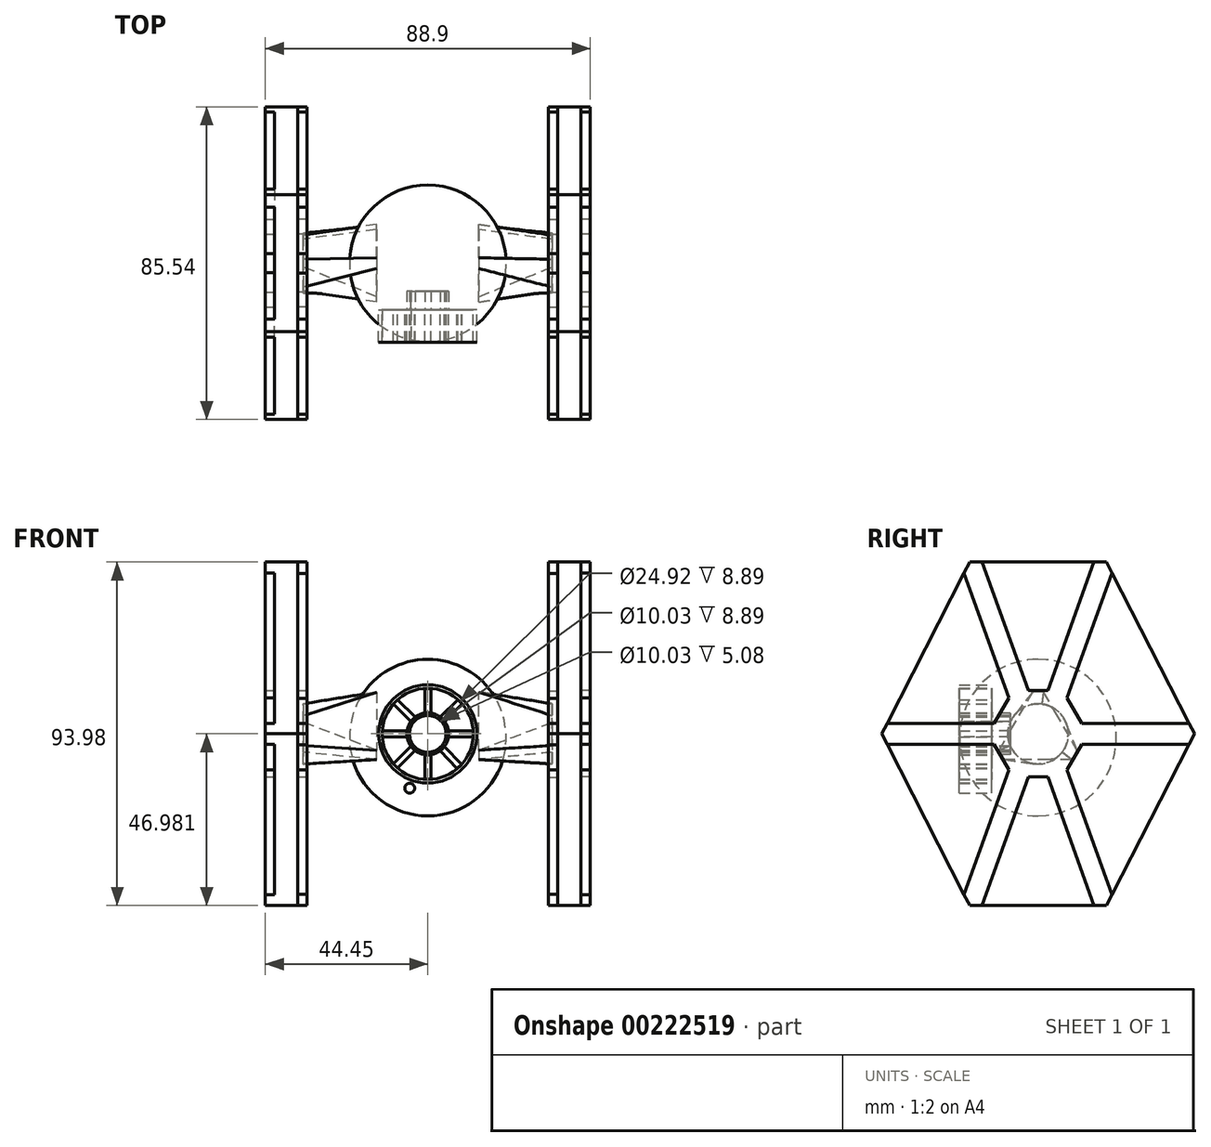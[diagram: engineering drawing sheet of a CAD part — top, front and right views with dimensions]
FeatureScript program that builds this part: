
annotation { "Feature Type Name" : "Feature", "Feature Type Description" : "" }
export const myFeature = defineFeature(function(context is Context, id is Id, definition is map)
    precondition{}
    {
        {
            var Q0;
            Q0=qCreatedBy(makeId("Right.planeOp"),FACE);
            cPlane(context, id + "F0", {"entities" : qUnion([Q0]), "cplaneType" : CPlaneType.OFFSET, "offset" : 38.1 * mm, "width" : 152.4 * mm, "height" : 152.4 * mm});
        }
        {
            var Q0;
            Q0=qCreatedBy(makeId("Right.planeOp"),FACE);
            var sketch = newSketch(context, id + "F1", { "sketchPlane" : qUnion([Q0])});
            skLineSegment(sketch, "E0.bottom", {"start": v(-18.68, -62.8) * mm, "end": v(18.68, -62.8) * mm});
            skPoint(sketch, "E0.middle", {"position": v(0, 0) * mm});
            skLineSegment(sketch, "E1", {"start": v(18.68, -62.8) * mm, "end": v(42.77, -15.81) * mm});
            skLineSegment(sketch, "E2.MirrorCS", {"start": v(-18.68, -62.8) * mm, "end": v(-42.77, -15.81) * mm});
            skLineSegment(sketch, "E3.MirrorCS", {"start": v(18.68, 31.18) * mm, "end": v(42.77, -15.81) * mm});
            skLineSegment(sketch, "E4.MirrorCS", {"start": v(-18.68, 31.18) * mm, "end": v(-42.77, -15.81) * mm});
            skLineSegment(sketch, "E5.MirrorCS", {"start": v(-18.68, 31.18) * mm, "end": v(18.68, 31.18) * mm});
            skSolve(sketch);
        }
        {
            var Q0;
            {var subQ1=sQuery(id+"F1.wireOp",EDGE,"E1");Q0=makeQuery(id+"F1.imprint","IMPRINT",FACE,{"disambiguationData":[TD([[makeQuery(id+"F1.imprint","IMPRINT",EDGE,{"derivedFrom":subQ1}),1.0]])]});}
            extrude(context, id + "F2", {"entities" : qUnion([Q0]), "depth" : 2.54 * mm});
        }
        {
            var Q0;
            Q0=makeQuery(id+"F2.opExtrude","CAP_FACE",FACE,{"disambiguationData":[OSD([sQuery(id+"F1.wireOp",EDGE,"E0.bottom"),sQuery(id+"F1.wireOp",EDGE,"E1"),sQuery(id+"F1.wireOp",EDGE,"E2.MirrorCS"),sQuery(id+"F1.wireOp",EDGE,"E3.MirrorCS"),sQuery(id+"F1.wireOp",EDGE,"E4.MirrorCS"),sQuery(id+"F1.wireOp",EDGE,"E5.MirrorCS"),sQuery(id+"F1.wireOp",EDGE,"2yPUHzrf-kxil-xjin-D1f0-5rGPGX8mDLb6.bottom"),sQuery(id+"F1.wireOp",EDGE,"2yPUHzrf-kxil-xjin-D1f0-5rGPGX8mDLb6.top")])],"isStart":false});
            var sketch = newSketch(context, id + "F3", { "sketchPlane" : qUnion([Q0])});
            skCircle(sketch, "E6", {"center": v(0, -15.81) * mm, "radius": 8.22 * mm});
            skSolve(sketch);
        }
        {
            var Q0;
            Q0=qCreatedBy(id+"F0.planeOp",FACE);
            var sketch = newSketch(context, id + "F4", { "sketchPlane" : qUnion([Q0])});
            skLineSegment(sketch, "E7", {"start": v(-0.03, 4.57) * mm, "end": v(0, -38.27) * mm});
            skArc(sketch, "E8", {"start": v(0, -38.27) * mm, "mid": v(21.4, -16.83) * mm, "end": v(-0.03, 4.57) * mm});
            skSolve(sketch);
        }
        {
            var Q0;
            Q0=makeQuery(id+"F2.opExtrude","CAP_FACE",FACE,{"disambiguationData":[OSD([sQuery(id+"F1.wireOp",EDGE,"E0.bottom"),sQuery(id+"F1.wireOp",EDGE,"E1"),sQuery(id+"F1.wireOp",EDGE,"E2.MirrorCS"),sQuery(id+"F1.wireOp",EDGE,"E3.MirrorCS"),sQuery(id+"F1.wireOp",EDGE,"E4.MirrorCS"),sQuery(id+"F1.wireOp",EDGE,"E5.MirrorCS")])],"isStart":true});
            var sketch = newSketch(context, id + "F5", { "sketchPlane" : qUnion([Q0])});
            skPoint(sketch, "E9.startSnap0", {"position": v(-5.35, -21.22) * mm});
            skSolve(sketch);
        }
        {
            var Q0;
            {var subQ1=sQuery(id+"F5.wireOp",EDGE,"249c2ce5-009a-41f7-bdd2-0ea9e0032ecc0.MirrorCS");var subQ6=makeQuery(id+"F2.opExtrude","CAP_EDGE",EDGE,{"disambiguationData":[OSD([sQuery(id+"F1.wireOp",EDGE,"E5.MirrorCS")])],"isStart":true});var subQ7=makeQuery(id+"F5.imprint","INTERSECT",VERTEX,{"derivedFrom":[subQ6,subQ1]});Q0=makeQuery(id+"F5.imprint","IMPRINT",FACE,{"disambiguationData":[TD([[makeQuery(id+"F5.imprint","IMPRINT",EDGE,{"disambiguationData":[TD([[subQ7,1.0]])],"derivedFrom":subQ6}),1.0]])]});}
            var Q1;
            {var subQ5=sQuery(id+"F5.wireOp",EDGE,"7VcF6iJS-dFkr-JtMG-80JM-9HORZD5tUdc8");Q1=makeQuery(id+"F5.imprint","IMPRINT",FACE,{"disambiguationData":[TD([[makeQuery(id+"F5.imprint","IMPRINT",EDGE,{"derivedFrom":subQ5}),-1.0]])]});}
            var Q2;
            {var subQ1=sQuery(id+"F5.wireOp",EDGE,"d53f9717-c929-49ff-bc3e-877c035910c40.MirrorCS");Q2=makeQuery(id+"F5.imprint","IMPRINT",FACE,{"disambiguationData":[TD([[makeQuery(id+"F5.imprint","IMPRINT",EDGE,{"derivedFrom":subQ1}),1.0]])]});}
            var Q3;
            {var subQ6=sQuery(id+"F5.wireOp",EDGE,"7JM50K66-Pmk8-nCnD-PpWn-c26iKmBIX4QO");var subQ9=sQuery(id+"F5.wireOp",EDGE,"93c2cfdc-00f6-405e-850a-5c9138fb73d70.MirrorC");var subQ11=makeQuery(id+"F5.imprint","INTERSECT",VERTEX,{"disambiguationData":[OD(0.0)],"derivedFrom":[subQ6,subQ9]});Q3=makeQuery(id+"F5.imprint","IMPRINT",FACE,{"disambiguationData":[TD([[makeQuery(id+"F5.imprint","IMPRINT",EDGE,{"disambiguationData":[TD([[subQ11,1.0]])],"derivedFrom":subQ9}),1.0]])]});}
            var Q4;
            {var subQ5=sQuery(id+"F5.wireOp",EDGE,"SASZ7VG5-cB94-bOMo-KIGx-b2qRhCJ8Sax1");Q4=makeQuery(id+"F5.imprint","IMPRINT",FACE,{"disambiguationData":[TD([[makeQuery(id+"F5.imprint","IMPRINT",EDGE,{"derivedFrom":subQ5}),1.0]])]});}
            var Q5;
            {var subQ0=sQuery(id+"F5.wireOp",EDGE,"HNDO0rkw-yRAK-74Ev-MwU3-I7vDTjC7gBuG");Q5=makeQuery(id+"F5.imprint","IMPRINT",FACE,{"disambiguationData":[TD([[makeQuery(id+"F5.imprint","IMPRINT",EDGE,{"derivedFrom":subQ0}),1.0]])]});}
            var Q6;
            {var subQ5=sQuery(id+"F5.wireOp",EDGE,"lByyAeW6-gkVC-xfzd-ToIX-et6EqGNpYPVb");Q6=makeQuery(id+"F5.imprint","IMPRINT",FACE,{"disambiguationData":[TD([[makeQuery(id+"F5.imprint","IMPRINT",EDGE,{"derivedFrom":subQ5}),-1.0]])]});}
            var Q7;
            {var subQ1=sQuery(id+"F5.wireOp",EDGE,"4a8b6011-c6cb-4acc-bbb3-d66b1ed156a90.MirrorCS");Q7=makeQuery(id+"F5.imprint","IMPRINT",FACE,{"disambiguationData":[TD([[makeQuery(id+"F5.imprint","IMPRINT",EDGE,{"derivedFrom":subQ1}),1.0]])]});}
            var Q8;
            {var subQ5=sQuery(id+"F5.wireOp",EDGE,"69e1f89e-e92b-4090-8e51-5caf598a36f10.MirrorCS");Q8=makeQuery(id+"F5.imprint","IMPRINT",FACE,{"disambiguationData":[TD([[makeQuery(id+"F5.imprint","IMPRINT",EDGE,{"derivedFrom":subQ5}),1.0]])]});}
            extrude(context, id + "F6", {"entities" : qUnion([Q0, Q1, Q2, Q3, Q4, Q5, Q6, Q7, Q8]), "operationType" : NewBodyOperationType.ADD, "depth" : 3.8 * mm});
        }
        {
            var Q0;
            Q0=qCreatedBy(makeId("Front.planeOp"),FACE);
            cPlane(context, id + "F7", {"entities" : qUnion([Q0]), "cplaneType" : CPlaneType.OFFSET, "offset" : 12.7 * mm, "width" : 152.4 * mm, "height" : 152.4 * mm});
        }
        {
            var Q0;
            Q0=makeQuery(id+"F2.opExtrude","SWEPT_BODY",BODY,{"disambiguationData":[OSD([sQuery(id+"F1.wireOp",EDGE,"E0.bottom"),sQuery(id+"F1.wireOp",EDGE,"E1"),sQuery(id+"F1.wireOp",EDGE,"E2.MirrorCS"),sQuery(id+"F1.wireOp",EDGE,"E3.MirrorCS"),sQuery(id+"F1.wireOp",EDGE,"E4.MirrorCS"),sQuery(id+"F1.wireOp",EDGE,"E5.MirrorCS"),sQuery(id+"F1.wireOp",EDGE,"2yPUHzrf-kxil-xjin-D1f0-5rGPGX8mDLb6.bottom"),sQuery(id+"F1.wireOp",EDGE,"2yPUHzrf-kxil-xjin-D1f0-5rGPGX8mDLb6.top")])]});
            var Q1;
            Q1=qCreatedBy(id+"F0.planeOp",FACE);
            mirror(context, id + "F8", {"entities" : qUnion([Q0]), "mirrorPlane" : qUnion([Q1])});
        }
        {
            var Q0;
            Q0=qCreatedBy(id+"F7.planeOp",FACE);
            var sketch = newSketch(context, id + "F9", { "sketchPlane" : qUnion([Q0])});
            skLineSegment(sketch, "E10", {"start": v(32.42, -15) * mm, "end": v(32.42, -16.63) * mm});
            skLineSegment(sketch, "E11.MirrorCS", {"start": v(43.78, -15) * mm, "end": v(43.78, -16.63) * mm});
            skCircle(sketch, "E12", {"center": v(38.1, -15.82) * mm, "radius": 5.74 * mm});
            skCircle(sketch, "E13", {"center": v(38.1, -15.82) * mm, "radius": 13.44 * mm});
            skCircle(sketch, "E14", {"center": v(38.1, -15.82) * mm, "radius": 12.46 * mm});
            skLineSegment(sketch, "E15", {"start": v(38.9, -28.25) * mm, "end": v(37.28, -28.25) * mm});
            skLineSegment(sketch, "E16", {"start": v(25.67, -15) * mm, "end": v(25.67, -16.63) * mm});
            skLineSegment(sketch, "E17", {"start": v(25.67, -16.63) * mm, "end": v(32.42, -16.63) * mm});
            skLineSegment(sketch, "E18", {"start": v(25.67, -15) * mm, "end": v(32.42, -15) * mm});
            skLineSegment(sketch, "E19", {"start": v(50.53, -15) * mm, "end": v(50.53, -16.63) * mm});
            skLineSegment(sketch, "E20", {"start": v(43.78, -16.63) * mm, "end": v(50.53, -16.63) * mm});
            skLineSegment(sketch, "E21", {"start": v(43.78, -15) * mm, "end": v(50.53, -15) * mm});
            skPoint(sketch, "E22.startSnap0", {"position": v(43.78, -15.82) * mm});
            skLineSegment(sketch, "E23", {"start": v(28.68, -23.97) * mm, "end": v(29.83, -25.14) * mm});
            skLineSegment(sketch, "E24", {"start": v(28.68, -23.97) * mm, "end": v(33.48, -19.23) * mm});
            skLineSegment(sketch, "E25", {"start": v(29.83, -25.14) * mm, "end": v(34.63, -20.4) * mm});
            skLineSegment(sketch, "E26", {"start": v(34.63, -20.4) * mm, "end": v(33.48, -19.23) * mm});
            skLineSegment(sketch, "E27", {"start": v(37.28, -28.25) * mm, "end": v(37.28, -21.5) * mm});
            skLineSegment(sketch, "E28", {"start": v(38.9, -28.25) * mm, "end": v(38.9, -21.5) * mm});
            skLineSegment(sketch, "E29", {"start": v(38.9, -21.5) * mm, "end": v(37.28, -21.5) * mm});
            skLineSegment(sketch, "E30", {"start": v(37.28, -10.14) * mm, "end": v(38.9, -10.14) * mm});
            skLineSegment(sketch, "E31", {"start": v(37.28, -10.14) * mm, "end": v(37.28, -3.38) * mm});
            skLineSegment(sketch, "E32", {"start": v(38.9, -10.14) * mm, "end": v(38.9, -3.38) * mm});
            skLineSegment(sketch, "E33", {"start": v(38.9, -3.38) * mm, "end": v(37.28, -3.38) * mm});
            skLineSegment(sketch, "E34.MirrorCS", {"start": v(46.37, -6.5) * mm, "end": v(41.57, -11.24) * mm});
            skLineSegment(sketch, "E35.MirrorCS", {"start": v(47.52, -7.66) * mm, "end": v(42.72, -12.4) * mm});
            skLineSegment(sketch, "E36.MirrorCS", {"start": v(42.72, -12.4) * mm, "end": v(41.57, -11.24) * mm});
            skLineSegment(sketch, "E37.MirrorCS", {"start": v(46.37, -6.5) * mm, "end": v(47.52, -7.66) * mm});
            skLineSegment(sketch, "E38.MirrorCS", {"start": v(29.83, -6.5) * mm, "end": v(34.63, -11.24) * mm});
            skLineSegment(sketch, "E39.MirrorCS", {"start": v(28.68, -7.66) * mm, "end": v(33.48, -12.4) * mm});
            skLineSegment(sketch, "E40.MirrorCS", {"start": v(33.48, -12.4) * mm, "end": v(34.63, -11.24) * mm});
            skLineSegment(sketch, "E41.MirrorCS", {"start": v(29.83, -6.5) * mm, "end": v(28.68, -7.66) * mm});
            skLineSegment(sketch, "E42.MirrorCS", {"start": v(47.32, -24.2) * mm, "end": v(42.63, -19.34) * mm});
            skLineSegment(sketch, "E43.MirrorCS", {"start": v(46.14, -25.34) * mm, "end": v(41.46, -20.48) * mm});
            skLineSegment(sketch, "E44.MirrorCS", {"start": v(47.32, -24.2) * mm, "end": v(46.14, -25.34) * mm});
            skLineSegment(sketch, "E45.MirrorCS", {"start": v(41.46, -20.48) * mm, "end": v(42.63, -19.34) * mm});
            skCircle(sketch, "E46", {"center": v(38.1, -15.82) * mm, "radius": 5.01 * mm});
            skSolve(sketch);
        }
        {
            var Q0;
            {var subQ14=sQuery(id+"F9.wireOp",EDGE,"73e59940-f8dd-450e-85ab-330bc53c69c60.MirrorCS");Q0=makeQuery(id+"F9.imprint","IMPRINT",FACE,{"disambiguationData":[TD([[makeQuery(id+"F9.imprint","IMPRINT",EDGE,{"derivedFrom":subQ14}),1.0]])]});}
            var Q1;
            {var subQ0=sQuery(id+"F9.wireOp",EDGE,"sVUFMM5y-C2RM-zDAE-oVfD-lKvkKs6ZE4KX");Q1=makeQuery(id+"F9.imprint","IMPRINT",FACE,{"disambiguationData":[TD([[makeQuery(id+"F9.imprint","IMPRINT",EDGE,{"derivedFrom":subQ0}),1.0]])]});}
            var Q2;
            {var subQ1=sQuery(id+"F9.wireOp",EDGE,"84d815f5-994e-4be1-8628-50fb4fe02ea00.MirrorCS");Q2=makeQuery(id+"F9.imprint","IMPRINT",FACE,{"disambiguationData":[TD([[makeQuery(id+"F9.imprint","IMPRINT",EDGE,{"derivedFrom":subQ1}),1.0]])]});}
            var Q3;
            {var subQ2=sQuery(id+"F9.wireOp",EDGE,"e3cf4e84-a14f-40f9-aafe-2878d3321a520.MirrorCS");Q3=makeQuery(id+"F9.imprint","IMPRINT",FACE,{"disambiguationData":[TD([[makeQuery(id+"F9.imprint","IMPRINT",EDGE,{"derivedFrom":subQ2}),-1.0]])]});}
            var Q4;
            {var subQ1=sQuery(id+"F9.wireOp",EDGE,"E10");Q4=makeQuery(id+"F9.imprint","IMPRINT",FACE,{"disambiguationData":[TD([[makeQuery(id+"F9.imprint","IMPRINT",EDGE,{"derivedFrom":subQ1}),1.0]])]});}
            var Q5;
            {var subQ5=sQuery(id+"F9.wireOp",EDGE,"nq8PGv4s-UvOK-GLhU-MlqA-lW3dcPxD6hmL");Q5=makeQuery(id+"F9.imprint","IMPRINT",FACE,{"disambiguationData":[TD([[makeQuery(id+"F9.imprint","IMPRINT",EDGE,{"derivedFrom":subQ5}),1.0]])]});}
            var Q6;
            Q6=makeQuery(id+"F9.imprint","IMPRINT",FACE,{"disambiguationData":[TD([[makeQuery(id+"F9.imprint","IMPRINT",EDGE,{"derivedFrom":sQuery(id+"F9.wireOp",EDGE,"kJPAYuFo-pbCG-mxDr-NveN-pNAolmRNOq98")}),1.0]])]});
            var Q7;
            {var subQ4=sQuery(id+"F9.wireOp",EDGE,"IcHEI2yc-UJXz-2Fey-pnqX-uZXjIdPkzv1H");Q7=makeQuery(id+"F9.imprint","IMPRINT",FACE,{"disambiguationData":[TD([[makeQuery(id+"F9.imprint","IMPRINT",EDGE,{"derivedFrom":subQ4}),1.0]])]});}
            var Q8;
            {var subQ0=sQuery(id+"F9.wireOp",EDGE,"6c8dea8c-eb7f-4e80-b223-ce5f32e7f4810.MirrorCS");Q8=makeQuery(id+"F9.imprint","IMPRINT",FACE,{"disambiguationData":[TD([[makeQuery(id+"F9.imprint","IMPRINT",EDGE,{"derivedFrom":subQ0}),-1.0]])]});}
            var Q9;
            {var subQ0=sQuery(id+"F9.wireOp",EDGE,"314743cd-5ef3-4182-b27c-d370bf35b7510.MirrorCS");Q9=makeQuery(id+"F9.imprint","IMPRINT",FACE,{"disambiguationData":[TD([[makeQuery(id+"F9.imprint","IMPRINT",EDGE,{"derivedFrom":subQ0}),1.0]])]});}
            extrude(context, id + "F10", {"entities" : qUnion([Q0, Q1, Q2, Q3, Q4, Q5, Q6, Q7, Q8, Q9]), "oppositeDirection" : true, "depth" : 5.08 * mm});
        }
        {
            var Q0;
            Q0=makeQuery(id+"F4.imprint","IMPRINT",FACE,{"disambiguationData":[TD([[makeQuery(id+"F4.imprint","IMPRINT",EDGE,{"derivedFrom":sQuery(id+"F4.wireOp",EDGE,"E7")}),1.0]])]});
            var Q1;
            Q1=sQuery(id+"F4.wireOp",EDGE,"E7");
            revolve(context, id + "F11", {"entities" : qUnion([Q0]), "axis" : qUnion([Q1]), "revolveType" : RevolveType.FULL});
        }
        {
            var Q0;
            {var subQ1=sQuery(id+"F9.wireOp",EDGE,"E38.MirrorCS");Q0=makeQuery(id+"F9.imprint","IMPRINT",FACE,{"disambiguationData":[TD([[makeQuery(id+"F9.imprint","IMPRINT",EDGE,{"derivedFrom":subQ1}),-1.0]])]});}
            var Q1;
            {var subQ0=sQuery(id+"F9.wireOp",EDGE,"E31");Q1=makeQuery(id+"F9.imprint","IMPRINT",FACE,{"disambiguationData":[TD([[makeQuery(id+"F9.imprint","IMPRINT",EDGE,{"derivedFrom":subQ0}),-1.0]])]});}
            var Q2;
            {var subQ1=sQuery(id+"F9.wireOp",EDGE,"E34.MirrorCS");Q2=makeQuery(id+"F9.imprint","IMPRINT",FACE,{"disambiguationData":[TD([[makeQuery(id+"F9.imprint","IMPRINT",EDGE,{"derivedFrom":subQ1}),1.0]])]});}
            var Q3;
            Q3=makeQuery(id+"F9.imprint","IMPRINT",FACE,{"disambiguationData":[TD([[makeQuery(id+"F9.imprint","IMPRINT",EDGE,{"derivedFrom":sQuery(id+"F9.wireOp",EDGE,"E19")}),-1.0]])]});
            var Q4;
            Q4=makeQuery(id+"F9.imprint","IMPRINT",FACE,{"disambiguationData":[TD([[makeQuery(id+"F9.imprint","IMPRINT",EDGE,{"derivedFrom":sQuery(id+"F9.wireOp",EDGE,"E15")}),-1.0]])]});
            var Q5;
            Q5=makeQuery(id+"F9.imprint","IMPRINT",FACE,{"disambiguationData":[TD([[makeQuery(id+"F9.imprint","IMPRINT",EDGE,{"derivedFrom":sQuery(id+"F9.wireOp",EDGE,"E23")}),1.0]])]});
            var Q6;
            {var subQ1=sQuery(id+"F9.wireOp",EDGE,"E42.MirrorCS");Q6=makeQuery(id+"F9.imprint","IMPRINT",FACE,{"disambiguationData":[TD([[makeQuery(id+"F9.imprint","IMPRINT",EDGE,{"derivedFrom":subQ1}),1.0]])]});}
            var Q7;
            Q7=makeQuery(id+"F9.imprint","IMPRINT",FACE,{"disambiguationData":[TD([[makeQuery(id+"F9.imprint","IMPRINT",EDGE,{"derivedFrom":sQuery(id+"F9.wireOp",EDGE,"E16")}),1.0]])]});
            var Q8;
            Q8=makeQuery(id+"F9.imprint","IMPRINT",FACE,{"disambiguationData":[TD([[makeQuery(id+"F9.imprint","IMPRINT",EDGE,{"derivedFrom":sQuery(id+"F9.wireOp",EDGE,"E13")}),1.0]])]});
            var Q9;
            {var subQ5=sQuery(id+"F9.wireOp",EDGE,"E10");Q9=makeQuery(id+"F9.imprint","IMPRINT",FACE,{"disambiguationData":[TD([[makeQuery(id+"F9.imprint","IMPRINT",EDGE,{"derivedFrom":subQ5}),1.0]])]});}
            extrude(context, id + "F12", {"entities" : qUnion([Q0, Q1, Q2, Q3, Q4, Q5, Q6, Q7, Q8, Q9]), "depth" : 8.9 * mm, "offsetDistance" : 25.4 * mm});
        }
        {
            var Q0;
            Q0=qCreatedBy(id+"F7.planeOp",FACE);
            var sketch = newSketch(context, id + "F13", { "sketchPlane" : qUnion([Q0])});
            skCircle(sketch, "E47", {"center": v(33.15, -30.69) * mm, "radius": 1.36 * mm});
            skCircle(sketch, "E48.MirrorC", {"center": v(43.05, -30.69) * mm, "radius": 1.36 * mm});
            skSolve(sketch);
        }
        {
            var Q0;
            Q0=makeQuery(id+"F13.imprint","IMPRINT",FACE,{"disambiguationData":[TD([[makeQuery(id+"F13.imprint","IMPRINT",EDGE,{"derivedFrom":sQuery(id+"F13.wireOp",EDGE,"E47")}),1.0]])]});
            var Q1;
            Q1=makeQuery(id+"F13.imprint","IMPRINT",FACE,{"disambiguationData":[TD([[makeQuery(id+"F13.imprint","IMPRINT",EDGE,{"derivedFrom":sQuery(id+"F13.wireOp",EDGE,"E48.MirrorC")}),-1.0]])]});
            extrude(context, id + "F14", {"entities" : qUnion([Q0, Q1]), "depth" : 8.9 * mm});
        }
        {
            var Q0;
            {var subQ0=sQuery(id+"F1.wireOp",EDGE,"E4.MirrorCS");Q0=makeQuery(id+"F17.boolean.opBoolean","SPLIT",FACE,{"disambiguationData":[TD([makeQuery(id+"F2.opExtrude","SWEPT_FACE",FACE,{"disambiguationData":[OSD([subQ0])]})])],"derivedFrom":makeQuery(id+"F6.opExtrude","CAP_FACE",FACE,{"disambiguationData":[OSD([sQuery(id+"F1.wireOp",EDGE,"E0.bottom"),sQuery(id+"F1.wireOp",EDGE,"E1"),sQuery(id+"F1.wireOp",EDGE,"E2.MirrorCS"),sQuery(id+"F1.wireOp",EDGE,"E3.MirrorCS"),subQ0,sQuery(id+"F1.wireOp",EDGE,"E5.MirrorCS")])],"isStart":false})});}
            cPlane(context, id + "F15", {"entities" : qUnion([Q0]), "cplaneType" : CPlaneType.OFFSET, "offset" : 0 * mm, "width" : 152.4 * mm, "height" : 152.4 * mm});
        }
        {
            var Q0;
            Q0=qCreatedBy(id+"F15.planeOp",FACE);
            var sketch = newSketch(context, id + "F16", { "sketchPlane" : qUnion([Q0])});
            skPoint(sketch, "E49.0.midPoint", {"position": v(0, -24.03) * mm});
            skLineSegment(sketch, "E50", {"start": v(-18.68, -62.8) * mm, "end": v(-20.23, -59.77) * mm});
            skLineSegment(sketch, "E51", {"start": v(-18.68, -62.8) * mm, "end": v(-15.28, -62.8) * mm});
            skLineSegment(sketch, "E52", {"start": v(-20.23, -59.77) * mm, "end": v(-7.97, -25.65) * mm});
            skLineSegment(sketch, "E53", {"start": v(-15.28, -62.8) * mm, "end": v(-2.64, -27.63) * mm});
            skLineSegment(sketch, "E54.MirrorCS", {"start": v(15.28, -62.8) * mm, "end": v(2.64, -27.63) * mm});
            skLineSegment(sketch, "E55.MirrorCS", {"start": v(20.23, -59.77) * mm, "end": v(7.97, -25.65) * mm});
            skLineSegment(sketch, "E56.MirrorCS", {"start": v(18.68, -62.8) * mm, "end": v(15.28, -62.8) * mm});
            skLineSegment(sketch, "E57.MirrorCS", {"start": v(18.68, -62.8) * mm, "end": v(20.23, -59.77) * mm});
            skLineSegment(sketch, "E58.MirrorCS", {"start": v(20.23, 28.14) * mm, "end": v(7.97, -5.98) * mm});
            skLineSegment(sketch, "E59.MirrorCS", {"start": v(15.28, 31.18) * mm, "end": v(2.64, -4) * mm});
            skLineSegment(sketch, "E60.MirrorCS", {"start": v(18.68, 31.18) * mm, "end": v(20.23, 28.14) * mm});
            skLineSegment(sketch, "E61.MirrorCS", {"start": v(18.68, 31.18) * mm, "end": v(15.28, 31.18) * mm});
            skLineSegment(sketch, "E62.MirrorCS", {"start": v(-20.23, 28.14) * mm, "end": v(-7.97, -5.98) * mm});
            skLineSegment(sketch, "E63.MirrorCS", {"start": v(-15.28, 31.18) * mm, "end": v(-2.64, -4) * mm});
            skLineSegment(sketch, "E64.MirrorCS", {"start": v(-18.68, 31.18) * mm, "end": v(-15.28, 31.18) * mm});
            skLineSegment(sketch, "E65.MirrorCS", {"start": v(-18.68, 31.18) * mm, "end": v(-20.23, 28.14) * mm});
            skLineSegment(sketch, "E66", {"start": v(-6.37, -21.2) * mm, "end": v(-1.35, -24.03) * mm});
            skLineSegment(sketch, "E67", {"start": v(1.35, -24.03) * mm, "end": v(6.37, -21.2) * mm});
            skLineSegment(sketch, "E68", {"start": v(-6.37, -10.42) * mm, "end": v(-1.35, -7.6) * mm});
            skLineSegment(sketch, "E69", {"start": v(1.35, -7.6) * mm, "end": v(6.37, -10.42) * mm});
            skLineSegment(sketch, "E70", {"start": v(-41.3, -12.93) * mm, "end": v(-42.77, -15.81) * mm});
            skLineSegment(sketch, "E71", {"start": v(-42.77, -15.81) * mm, "end": v(-41.3, -18.7) * mm});
            skLineSegment(sketch, "E72", {"start": v(-41.3, -12.93) * mm, "end": v(-11.98, -12.93) * mm});
            skLineSegment(sketch, "E73", {"start": v(-41.3, -18.7) * mm, "end": v(-11.98, -18.7) * mm});
            skLineSegment(sketch, "E74", {"start": v(-7.7, -18.7) * mm, "end": v(-7.7, -12.93) * mm});
            skLineSegment(sketch, "E75.MirrorCS", {"start": v(41.3, -12.93) * mm, "end": v(11.98, -12.93) * mm});
            skLineSegment(sketch, "E76.MirrorCS", {"start": v(41.3, -18.7) * mm, "end": v(11.98, -18.7) * mm});
            skLineSegment(sketch, "E77.MirrorCS", {"start": v(7.7, -18.7) * mm, "end": v(7.7, -12.93) * mm});
            skLineSegment(sketch, "E78.MirrorCS", {"start": v(42.77, -15.81) * mm, "end": v(41.3, -18.7) * mm});
            skLineSegment(sketch, "E79.MirrorCS", {"start": v(41.3, -12.93) * mm, "end": v(42.77, -15.81) * mm});
            skLineSegment(sketch, "E80", {"start": v(-7.7, -18.7) * mm, "end": v(-6.37, -21.2) * mm});
            skLineSegment(sketch, "E81", {"start": v(-7.7, -12.93) * mm, "end": v(-6.37, -10.42) * mm});
            skLineSegment(sketch, "E82", {"start": v(-1.35, -7.6) * mm, "end": v(1.35, -7.6) * mm});
            skLineSegment(sketch, "E83", {"start": v(6.37, -10.42) * mm, "end": v(7.7, -12.93) * mm});
            skLineSegment(sketch, "E84", {"start": v(6.37, -21.2) * mm, "end": v(7.7, -18.7) * mm});
            skLineSegment(sketch, "E85", {"start": v(-1.35, -24.03) * mm, "end": v(1.35, -24.03) * mm});
            skLineSegment(sketch, "E86.0", {"start": v(6.82, -27.63) * mm, "end": v(-6.82, -27.63) * mm});
            skLineSegment(sketch, "E86.1", {"start": v(-6.82, -27.63) * mm, "end": v(-13.64, -15.81) * mm});
            skLineSegment(sketch, "E86.2", {"start": v(-13.64, -15.81) * mm, "end": v(-6.82, -4) * mm});
            skLineSegment(sketch, "E86.3", {"start": v(-6.82, -4) * mm, "end": v(6.82, -4) * mm});
            skLineSegment(sketch, "E86.4", {"start": v(6.82, -4) * mm, "end": v(13.64, -15.81) * mm});
            skLineSegment(sketch, "E86.5", {"start": v(13.64, -15.81) * mm, "end": v(6.82, -27.63) * mm});
            skPoint(sketch, "E86.0.midPoint", {"position": v(0, -27.63) * mm});
            skSolve(sketch);
        }
        {
            var Q0;
            Q0=makeQuery(id+"F16.imprint","IMPRINT",FACE,{"disambiguationData":[TD([[makeQuery(id+"F16.imprint","IMPRINT",EDGE,{"derivedFrom":sQuery(id+"F16.wireOp",EDGE,"E70")}),1.0]])]});
            var Q1;
            Q1=makeQuery(id+"F16.imprint","IMPRINT",FACE,{"disambiguationData":[TD([[makeQuery(id+"F16.imprint","IMPRINT",EDGE,{"derivedFrom":sQuery(id+"F16.wireOp",EDGE,"E66")}),1.0]])]});
            var Q2;
            Q2=makeQuery(id+"F16.imprint","IMPRINT",FACE,{"disambiguationData":[TD([[makeQuery(id+"F16.imprint","IMPRINT",EDGE,{"derivedFrom":sQuery(id+"F16.wireOp",EDGE,"E58.MirrorCS")}),-1.0]])]});
            var Q3;
            Q3=makeQuery(id+"F16.imprint","IMPRINT",FACE,{"disambiguationData":[TD([[makeQuery(id+"F16.imprint","IMPRINT",EDGE,{"derivedFrom":sQuery(id+"F16.wireOp",EDGE,"E62.MirrorCS")}),1.0]])]});
            var Q4;
            Q4=makeQuery(id+"F16.imprint","IMPRINT",FACE,{"disambiguationData":[TD([[makeQuery(id+"F16.imprint","IMPRINT",EDGE,{"derivedFrom":sQuery(id+"F16.wireOp",EDGE,"E75.MirrorCS")}),1.0]])]});
            var Q5;
            Q5=makeQuery(id+"F16.imprint","IMPRINT",FACE,{"disambiguationData":[TD([[makeQuery(id+"F16.imprint","IMPRINT",EDGE,{"derivedFrom":sQuery(id+"F16.wireOp",EDGE,"E54.MirrorCS")}),-1.0]])]});
            var Q6;
            Q6=makeQuery(id+"F16.imprint","IMPRINT",FACE,{"disambiguationData":[TD([[makeQuery(id+"F16.imprint","IMPRINT",EDGE,{"derivedFrom":sQuery(id+"F16.wireOp",EDGE,"E50")}),-1.0]])]});
            var Q7;
            Q7=makeQuery(id+"F16.imprint","IMPRINT",FACE,{"disambiguationData":[TD([[makeQuery(id+"F16.imprint","IMPRINT",EDGE,{"derivedFrom":sQuery(id+"F16.wireOp",EDGE,"E66")}),-1.0]])]});
            extrude(context, id + "F17", {"entities" : qUnion([Q0, Q1, Q2, Q3, Q4, Q5, Q6, Q7]), "operationType" : NewBodyOperationType.ADD, "depth" : 2.54 * mm});
        }
        {
            var Q0;
            Q0=makeQuery(id+"F2.opExtrude","SWEPT_BODY",BODY,{"disambiguationData":[OSD([sQuery(id+"F1.wireOp",EDGE,"E0.bottom"),sQuery(id+"F1.wireOp",EDGE,"E1"),sQuery(id+"F1.wireOp",EDGE,"E2.MirrorCS"),sQuery(id+"F1.wireOp",EDGE,"E3.MirrorCS"),sQuery(id+"F1.wireOp",EDGE,"E4.MirrorCS"),sQuery(id+"F1.wireOp",EDGE,"E5.MirrorCS")])]});
            var Q1;
            Q1=qCreatedBy(id+"F0.planeOp",FACE);
            mirror(context, id + "F18", {"entities" : qUnion([Q0]), "mirrorPlane" : qUnion([Q1])});
        }
        {
            var Q0;
            Q0=makeQuery(id+"F3.imprint","IMPRINT",FACE,{"disambiguationData":[TD([[makeQuery(id+"F3.imprint","IMPRINT",EDGE,{"derivedFrom":sQuery(id+"F3.wireOp",EDGE,"E6")}),-1.0]])]});
            var sketch = newSketch(context, id + "F19", { "sketchPlane" : qUnion([Q0])});
            skPoint(sketch, "E87.0.midPoint", {"position": v(-0.03, -24.09) * mm});
            skLineSegment(sketch, "E88", {"start": v(-18.73, -62.91) * mm, "end": v(-20.29, -59.88) * mm});
            skLineSegment(sketch, "E89", {"start": v(-18.73, -62.91) * mm, "end": v(-15.33, -62.91) * mm});
            skLineSegment(sketch, "E90", {"start": v(-20.29, -59.88) * mm, "end": v(-7.98, -25.63) * mm});
            skLineSegment(sketch, "E91", {"start": v(-15.33, -62.91) * mm, "end": v(-2.66, -27.65) * mm});
            skLineSegment(sketch, "E92.MirrorCS", {"start": v(15.27, -62.91) * mm, "end": v(2.6, -27.65) * mm});
            skLineSegment(sketch, "E93.MirrorCS", {"start": v(20.23, -59.88) * mm, "end": v(7.95, -25.7) * mm});
            skLineSegment(sketch, "E94.MirrorCS", {"start": v(18.67, -62.91) * mm, "end": v(15.27, -62.91) * mm});
            skLineSegment(sketch, "E95.MirrorCS", {"start": v(18.67, -62.91) * mm, "end": v(20.23, -59.88) * mm});
            skLineSegment(sketch, "E96.MirrorCS", {"start": v(20.23, 28.16) * mm, "end": v(7.96, -6) * mm});
            skLineSegment(sketch, "E97.MirrorCS", {"start": v(15.27, 31.2) * mm, "end": v(2.61, -4.02) * mm});
            skLineSegment(sketch, "E98.MirrorCS", {"start": v(18.67, 31.2) * mm, "end": v(20.23, 28.16) * mm});
            skLineSegment(sketch, "E99.MirrorCS", {"start": v(18.67, 31.2) * mm, "end": v(15.27, 31.2) * mm});
            skLineSegment(sketch, "E100.MirrorCS", {"start": v(-20.29, 28.16) * mm, "end": v(-8, -6.06) * mm});
            skLineSegment(sketch, "E101.MirrorCS", {"start": v(-15.33, 31.2) * mm, "end": v(-2.68, -4.02) * mm});
            skLineSegment(sketch, "E102.MirrorCS", {"start": v(-18.73, 31.2) * mm, "end": v(-15.33, 31.2) * mm});
            skLineSegment(sketch, "E103.MirrorCS", {"start": v(-18.73, 31.2) * mm, "end": v(-20.29, 28.16) * mm});
            skLineSegment(sketch, "E104", {"start": v(-41.38, -12.97) * mm, "end": v(-42.86, -15.86) * mm});
            skLineSegment(sketch, "E105", {"start": v(-42.86, -15.86) * mm, "end": v(-41.38, -18.75) * mm});
            skLineSegment(sketch, "E106", {"start": v(-41.38, -12.97) * mm, "end": v(-11.99, -12.97) * mm});
            skLineSegment(sketch, "E107", {"start": v(-41.38, -18.75) * mm, "end": v(-11.96, -18.75) * mm});
            skLineSegment(sketch, "E108.MirrorCS", {"start": v(41.32, -12.97) * mm, "end": v(11.99, -12.97) * mm});
            skLineSegment(sketch, "E109.MirrorCS", {"start": v(41.32, -18.75) * mm, "end": v(11.96, -18.75) * mm});
            skLineSegment(sketch, "E110.MirrorCS", {"start": v(42.8, -15.86) * mm, "end": v(41.32, -18.75) * mm});
            skLineSegment(sketch, "E111.MirrorCS", {"start": v(41.32, -12.97) * mm, "end": v(42.8, -15.86) * mm});
            skLineSegment(sketch, "E112.0", {"start": v(6.82, -27.65) * mm, "end": v(-6.82, -27.65) * mm});
            skLineSegment(sketch, "E112.1", {"start": v(-6.82, -27.65) * mm, "end": v(-13.64, -15.84) * mm});
            skLineSegment(sketch, "E112.2", {"start": v(-13.64, -15.84) * mm, "end": v(-6.82, -4.02) * mm});
            skLineSegment(sketch, "E112.3", {"start": v(-6.82, -4.02) * mm, "end": v(6.82, -4.02) * mm});
            skLineSegment(sketch, "E112.4", {"start": v(6.82, -4.02) * mm, "end": v(13.64, -15.84) * mm});
            skLineSegment(sketch, "E112.5", {"start": v(13.64, -15.84) * mm, "end": v(6.82, -27.65) * mm});
            skPoint(sketch, "E112.0.midPoint", {"position": v(0, -27.65) * mm});
            skSolve(sketch);
        }
        {
            var Q0;
            {var subQ0=sQuery(id+"F19.wireOp",EDGE,"E112.1");var subQ1=sQuery(id+"F19.wireOp",EDGE,"E90");var subQ2=makeQuery(id+"F19.imprint","INTERSECT",VERTEX,{"derivedFrom":[subQ1,subQ0]});Q0=makeQuery(id+"F19.imprint","IMPRINT",FACE,{"disambiguationData":[TD([[makeQuery(id+"F19.imprint","IMPRINT",EDGE,{"disambiguationData":[TD([[subQ2,1.0]])],"derivedFrom":subQ1}),-1.0]])]});}
            var Q1;
            {var subQ3=sQuery(id+"F19.wireOp",EDGE,"E112.2");var subQ9=sQuery(id+"F19.wireOp",EDGE,"E106");var subQ10=makeQuery(id+"F19.imprint","INTERSECT",VERTEX,{"derivedFrom":[subQ9,subQ3]});Q1=makeQuery(id+"F19.imprint","IMPRINT",FACE,{"disambiguationData":[TD([[makeQuery(id+"F19.imprint","IMPRINT",EDGE,{"disambiguationData":[TD([[subQ10,1.0]])],"derivedFrom":subQ9}),-1.0]])]});}
            var Q2;
            {var subQ3=sQuery(id+"F19.wireOp",EDGE,"E112.4");var subQ7=sQuery(id+"F19.wireOp",EDGE,"E96.MirrorCS");var subQ8=makeQuery(id+"F19.imprint","INTERSECT",VERTEX,{"derivedFrom":[subQ7,subQ3]});Q2=makeQuery(id+"F19.imprint","IMPRINT",FACE,{"disambiguationData":[TD([[makeQuery(id+"F19.imprint","IMPRINT",EDGE,{"disambiguationData":[TD([[subQ8,1.0]])],"derivedFrom":subQ7}),-1.0]])]});}
            var Q3;
            {var subQ0=sQuery(id+"F19.wireOp",EDGE,"E112.4");var subQ1=sQuery(id+"F19.wireOp",EDGE,"E108.MirrorCS");var subQ2=makeQuery(id+"F19.imprint","INTERSECT",VERTEX,{"derivedFrom":[subQ1,subQ0]});Q3=makeQuery(id+"F19.imprint","IMPRINT",FACE,{"disambiguationData":[TD([[makeQuery(id+"F19.imprint","IMPRINT",EDGE,{"disambiguationData":[TD([[subQ2,1.0]])],"derivedFrom":subQ1}),1.0]])]});}
            var Q4;
            {var subQ3=sQuery(id+"F19.wireOp",EDGE,"E112.2");var subQ7=sQuery(id+"F19.wireOp",EDGE,"E100.MirrorCS");var subQ8=makeQuery(id+"F19.imprint","INTERSECT",VERTEX,{"derivedFrom":[subQ7,subQ3]});Q4=makeQuery(id+"F19.imprint","IMPRINT",FACE,{"disambiguationData":[TD([[makeQuery(id+"F19.imprint","IMPRINT",EDGE,{"disambiguationData":[TD([[subQ8,1.0]])],"derivedFrom":subQ7}),1.0]])]});}
            var Q5;
            Q5=makeQuery(id+"F19.imprint","IMPRINT",FACE,{"disambiguationData":[TD([[makeQuery(id+"F19.imprint","IMPRINT",EDGE,{"derivedFrom":makeQuery(id+"F3.imprint","IMPRINT",EDGE,{"derivedFrom":sQuery(id+"F3.wireOp",EDGE,"E6")})}),-1.0]])]});
            var Q6;
            Q6=makeQuery(id+"F19.imprint","IMPRINT",FACE,{"disambiguationData":[TD([[makeQuery(id+"F19.imprint","IMPRINT",EDGE,{"derivedFrom":makeQuery(id+"F3.imprint","IMPRINT",EDGE,{"derivedFrom":sQuery(id+"F3.wireOp",EDGE,"E6")})}),1.0]])]});
            var Q7;
            {var subQ3=sQuery(id+"F19.wireOp",EDGE,"E112.0");var subQ7=sQuery(id+"F19.wireOp",EDGE,"E92.MirrorCS");var subQ8=makeQuery(id+"F19.imprint","INTERSECT",VERTEX,{"derivedFrom":[subQ7,subQ3]});Q7=makeQuery(id+"F19.imprint","IMPRINT",FACE,{"disambiguationData":[TD([[makeQuery(id+"F19.imprint","IMPRINT",EDGE,{"disambiguationData":[TD([[subQ8,1.0]])],"derivedFrom":subQ7}),-1.0]])]});}
            extrude(context, id + "F20", {"entities" : qUnion([Q0, Q1, Q2, Q3, Q4, Q5, Q6, Q7]), "depth" : 2.54 * mm, "offsetDistance" : 25.4 * mm});
        }
        {
            var Q0;
            Q0=makeQuery(id+"F20.opExtrude","SWEPT_BODY",BODY,{"disambiguationData":[OSD([sQuery(id+"F1.wireOp",EDGE,"E2.MirrorCS"),sQuery(id+"F1.wireOp",EDGE,"E4.MirrorCS"),sQuery(id+"F3.wireOp",EDGE,"E6"),sQuery(id+"F19.wireOp",EDGE,"E106"),sQuery(id+"F19.wireOp",EDGE,"E107"),sQuery(id+"F19.wireOp",EDGE,"2aa20023-c7b0-4b2b-915d-71bae8cab18d")])]});
            var Q1;
            Q1=makeQuery(id+"F20.opExtrude","SWEPT_BODY",BODY,{"disambiguationData":[OSD([sQuery(id+"F3.wireOp",EDGE,"E6")])]});
            var Q2;
            Q2=makeQuery(id+"F20.opExtrude","SWEPT_BODY",BODY,{"disambiguationData":[OSD([sQuery(id+"F1.wireOp",EDGE,"E4.MirrorCS"),sQuery(id+"F3.wireOp",EDGE,"E6"),sQuery(id+"F19.wireOp",EDGE,"E100.MirrorCS"),sQuery(id+"F19.wireOp",EDGE,"E101.MirrorCS"),sQuery(id+"F19.wireOp",EDGE,"E102.MirrorCS"),sQuery(id+"F19.wireOp",EDGE,"7af6e436-8d5a-4fc4-bd95-5afbcdf9ebc1")])]});
            var Q3;
            Q3=makeQuery(id+"F20.opExtrude","SWEPT_BODY",BODY,{"disambiguationData":[OSD([sQuery(id+"F3.wireOp",EDGE,"E6"),sQuery(id+"F19.wireOp",EDGE,"E96.MirrorCS"),sQuery(id+"F19.wireOp",EDGE,"E97.MirrorCS"),sQuery(id+"F19.wireOp",EDGE,"E98.MirrorCS"),sQuery(id+"F19.wireOp",EDGE,"E99.MirrorCS"),sQuery(id+"F19.wireOp",EDGE,"c8762eaa-3f5d-43dd-ad10-f707925b9254")])]});
            var Q4;
            Q4=makeQuery(id+"F20.opExtrude","SWEPT_BODY",BODY,{"disambiguationData":[OSD([sQuery(id+"F1.wireOp",EDGE,"E0.bottom"),sQuery(id+"F1.wireOp",EDGE,"E2.MirrorCS"),sQuery(id+"F3.wireOp",EDGE,"E6"),sQuery(id+"F19.wireOp",EDGE,"E90"),sQuery(id+"F19.wireOp",EDGE,"E91"),sQuery(id+"F19.wireOp",EDGE,"dfccf998-6865-4125-a587-a97a453d0cde")])]});
            var Q5;
            Q5=makeQuery(id+"F20.opExtrude","SWEPT_BODY",BODY,{"disambiguationData":[OSD([sQuery(id+"F1.wireOp",EDGE,"E0.bottom"),sQuery(id+"F3.wireOp",EDGE,"E6"),sQuery(id+"F19.wireOp",EDGE,"E92.MirrorCS"),sQuery(id+"F19.wireOp",EDGE,"E93.MirrorCS"),sQuery(id+"F19.wireOp",EDGE,"E95.MirrorCS"),sQuery(id+"F19.wireOp",EDGE,"cf72e361-4477-4e51-9806-6e20ddd057b3")])]});
            var Q6;
            Q6=makeQuery(id+"F20.opExtrude","SWEPT_BODY",BODY,{"disambiguationData":[OSD([sQuery(id+"F3.wireOp",EDGE,"E6"),sQuery(id+"F19.wireOp",EDGE,"E108.MirrorCS"),sQuery(id+"F19.wireOp",EDGE,"E109.MirrorCS"),sQuery(id+"F19.wireOp",EDGE,"E110.MirrorCS"),sQuery(id+"F19.wireOp",EDGE,"E111.MirrorCS")])]});
            var Q7;
            Q7=qCreatedBy(id+"F0.planeOp",FACE);
            mirror(context, id + "F21", {"entities" : qUnion([Q0, Q1, Q2, Q3, Q4, Q5, Q6]), "mirrorPlane" : qUnion([Q7])});
        }
        {
            var Q0;
            Q0=qCreatedBy(makeId("Right.planeOp"),FACE);
            cPlane(context, id + "F22", {"entities" : qUnion([Q0]), "cplaneType" : CPlaneType.OFFSET, "offset" : 24.13 * mm, "width" : 152.4 * mm, "height" : 152.4 * mm});
        }
        {
            var Q0;
            Q0=qCreatedBy(id+"F0.planeOp",FACE);
            cPlane(context, id + "F23", {"entities" : qUnion([Q0]), "cplaneType" : CPlaneType.OFFSET, "offset" : 34.04 * mm, "oppositeDirection" : true, "width" : 152.4 * mm, "height" : 152.4 * mm});
        }
        {
            var Q0;
            Q0=makeQuery(id+"F20.opExtrude","SWEPT_BODY",BODY,{"disambiguationData":[OSD([sQuery(id+"F1.wireOp",EDGE,"E0.bottom"),sQuery(id+"F1.wireOp",EDGE,"E2.MirrorCS"),sQuery(id+"F1.wireOp",EDGE,"E4.MirrorCS"),sQuery(id+"F3.wireOp",EDGE,"E6"),sQuery(id+"F19.wireOp",EDGE,"E90"),sQuery(id+"F19.wireOp",EDGE,"E91"),sQuery(id+"F19.wireOp",EDGE,"E92.MirrorCS"),sQuery(id+"F19.wireOp",EDGE,"E93.MirrorCS"),sQuery(id+"F19.wireOp",EDGE,"E94.MirrorCS"),sQuery(id+"F19.wireOp",EDGE,"E95.MirrorCS"),sQuery(id+"F19.wireOp",EDGE,"E96.MirrorCS"),sQuery(id+"F19.wireOp",EDGE,"E97.MirrorCS"),sQuery(id+"F19.wireOp",EDGE,"E98.MirrorCS"),sQuery(id+"F19.wireOp",EDGE,"E99.MirrorCS"),sQuery(id+"F19.wireOp",EDGE,"E100.MirrorCS"),sQuery(id+"F19.wireOp",EDGE,"E101.MirrorCS"),sQuery(id+"F19.wireOp",EDGE,"E102.MirrorCS"),sQuery(id+"F19.wireOp",EDGE,"E103.MirrorCS"),sQuery(id+"F19.wireOp",EDGE,"dfccf998-6865-4125-a587-a97a453d0cde"),sQuery(id+"F19.wireOp",EDGE,"cf72e361-4477-4e51-9806-6e20ddd057b3"),sQuery(id+"F19.wireOp",EDGE,"7af6e436-8d5a-4fc4-bd95-5afbcdf9ebc1"),sQuery(id+"F19.wireOp",EDGE,"c8762eaa-3f5d-43dd-ad10-f707925b9254"),sQuery(id+"F19.wireOp",EDGE,"E106"),sQuery(id+"F19.wireOp",EDGE,"E107"),sQuery(id+"F19.wireOp",EDGE,"2aa20023-c7b0-4b2b-915d-71bae8cab18d"),sQuery(id+"F19.wireOp",EDGE,"E108.MirrorCS"),sQuery(id+"F19.wireOp",EDGE,"E109.MirrorCS"),sQuery(id+"F19.wireOp",EDGE,"E110.MirrorCS"),sQuery(id+"F19.wireOp",EDGE,"E111.MirrorCS"),sQuery(id+"F19.wireOp",EDGE,"550c9601-f962-46f9-9c83-c8b029b163b3"),sQuery(id+"F19.wireOp",EDGE,"b20fee39-5586-4955-9534-c2a9ec9fea09"),sQuery(id+"F19.wireOp",EDGE,"27bc3c62-9a52-47a2-9c4c-0584f26aff62"),sQuery(id+"F19.wireOp",EDGE,"a24cf038-79ec-41bc-93fe-006415d22749"),sQuery(id+"F19.wireOp",EDGE,"1f71c36f-1ea0-4032-9235-c50a7104aa7d"),sQuery(id+"F19.wireOp",EDGE,"25d197da-c755-48c5-9b52-b999f5c48841"),sQuery(id+"F19.wireOp",EDGE,"E112.0"),sQuery(id+"F19.wireOp",EDGE,"E112.1"),sQuery(id+"F19.wireOp",EDGE,"E112.2"),sQuery(id+"F19.wireOp",EDGE,"E112.3"),sQuery(id+"F19.wireOp",EDGE,"E112.4"),sQuery(id+"F19.wireOp",EDGE,"E112.5")])]});
            var Q1;
            Q1=qCreatedBy(id+"F0.planeOp",FACE);
            mirror(context, id + "F24", {"entities" : qUnion([Q0]), "mirrorPlane" : qUnion([Q1])});
        }
        {
            var Q0;
            Q0=qCreatedBy(id+"F23.planeOp",FACE);
            var sketch = newSketch(context, id + "F25", { "sketchPlane" : qUnion([Q0])});
            skCircle(sketch, "E113", {"center": v(0, -15.84) * mm, "radius": 8.25 * mm});
            skSolve(sketch);
        }
        {
            var Q0;
            Q0=qCreatedBy(id+"F22.planeOp",FACE);
            var sketch = newSketch(context, id + "F26", { "sketchPlane" : qUnion([Q0])});
            skCircle(sketch, "E114", {"center": v(0, -15.84) * mm, "radius": 11.53 * mm});
            skLineSegment(sketch, "E115.0", {"start": v(12.12, -22.83) * mm, "end": v(-12.12, -22.83) * mm});
            skLineSegment(sketch, "E115.1", {"start": v(-12.12, -22.83) * mm, "end": v(0, -1.84) * mm});
            skLineSegment(sketch, "E115.2", {"start": v(0, -1.84) * mm, "end": v(12.12, -22.83) * mm});
            skPoint(sketch, "E115.0.midPoint", {"position": v(0, -22.83) * mm});
            skSolve(sketch);
        }
        {
            var Q0;
            Q0=makeQuery(id+"F26.imprint","IMPRINT",FACE,{"disambiguationData":[TD([[makeQuery(id+"F26.imprint","IMPRINT",EDGE,{"derivedFrom":sQuery(id+"F26.wireOp",EDGE,"E114")}),1.0]])]});
            var Q1;
            Q1=makeQuery(id+"F25.imprint","IMPRINT",FACE,{"disambiguationData":[TD([[makeQuery(id+"F25.imprint","IMPRINT",EDGE,{"derivedFrom":sQuery(id+"F25.wireOp",EDGE,"E113")}),1.0]])]});
            loft(context, id + "F27", {"sheetProfilesArray" : [{ "sheetProfileEntities" : qUnion([Q0]) }, { "sheetProfileEntities" : qUnion([Q1]) }]});
        }
        {
            var Q0;
            Q0=makeQuery(id+"F27.opLoft","SWEPT_BODY",BODY,{"disambiguationData":[OSD([makeQuery(id+"F25.imprint","IMPRINT",FACE,{"disambiguationData":[TD([[makeQuery(id+"F25.imprint","IMPRINT",EDGE,{"derivedFrom":sQuery(id+"F25.wireOp",EDGE,"E113")}),1.0]])]}),makeQuery(id+"F26.imprint","IMPRINT",FACE,{"disambiguationData":[TD([[makeQuery(id+"F26.imprint","IMPRINT",EDGE,{"derivedFrom":sQuery(id+"F26.wireOp",EDGE,"E114")}),1.0]])]})])]});
            var Q1;
            Q1=qCreatedBy(id+"F0.planeOp",FACE);
            mirror(context, id + "F28", {"entities" : qUnion([Q0]), "mirrorPlane" : qUnion([Q1])});
        }
    });
